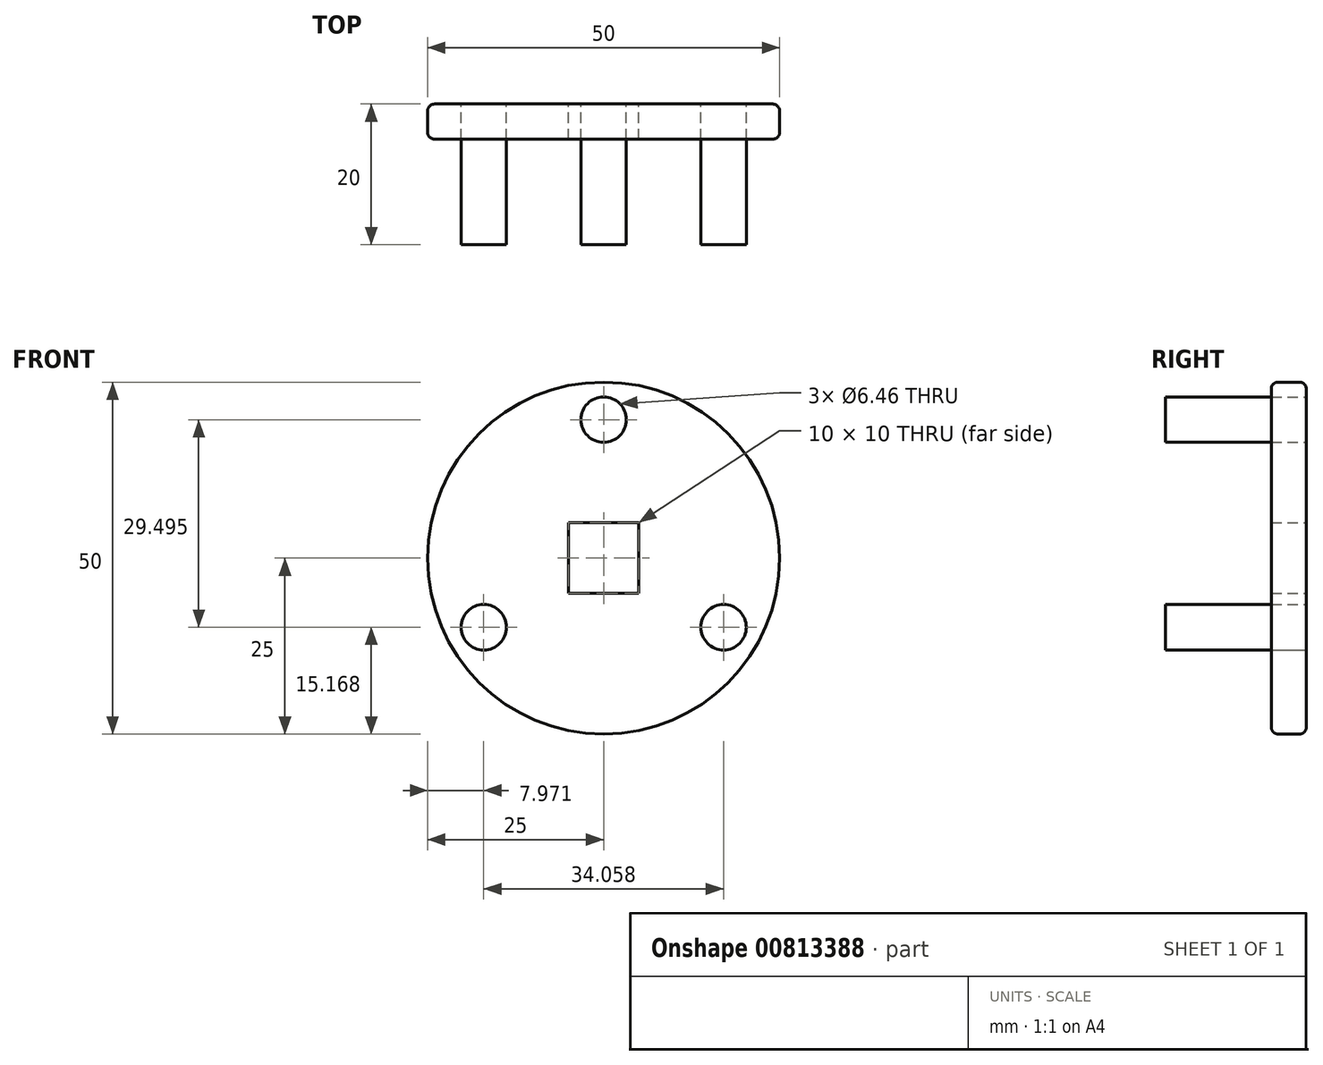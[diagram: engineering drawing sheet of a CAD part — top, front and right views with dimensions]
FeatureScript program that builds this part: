
annotation { "Feature Type Name" : "Feature", "Feature Type Description" : "" }
export const myFeature = defineFeature(function(context is Context, id is Id, definition is map)
    precondition{}
    {
        {
            var Q0;
            Q0=qCreatedBy(makeId("Front.planeOp"),FACE);
            var sketch = newSketch(context, id + "F0", { "sketchPlane" : qUnion([Q0])});
            skCircle(sketch, "E0", {"center": v(0, 0) * mm, "radius": 25 * mm});
            skCircle(sketch, "E1", {"center": v(0, 19.66) * mm, "radius": 3.23 * mm});
            skCircle(sketch, "E2.1.0", {"center": v(-17.03, -9.83) * mm, "radius": 3.23 * mm});
            skCircle(sketch, "E2.2.0", {"center": v(17.03, -9.83) * mm, "radius": 3.23 * mm});
            skLineSegment(sketch, "E3.bottom", {"start": v(-5, -5) * mm, "end": v(5, -5) * mm});
            skLineSegment(sketch, "E3.top", {"start": v(-5, 5) * mm, "end": v(5, 5) * mm});
            skLineSegment(sketch, "E3.left", {"start": v(-5, -5) * mm, "end": v(-5, 5) * mm});
            skLineSegment(sketch, "E3.right", {"start": v(5, -5) * mm, "end": v(5, 5) * mm});
            skSolve(sketch);
        }
        {
            var Q0;
            Q0=makeQuery(id+"F0.imprint","IMPRINT",FACE,{"disambiguationData":[TD([[makeQuery(id+"F0.imprint","IMPRINT",EDGE,{"derivedFrom":sQuery(id+"F0.wireOp",EDGE,"E2.2.0")}),1.0]])]});
            var Q1;
            Q1=makeQuery(id+"F0.imprint","IMPRINT",FACE,{"disambiguationData":[TD([[makeQuery(id+"F0.imprint","IMPRINT",EDGE,{"derivedFrom":sQuery(id+"F0.wireOp",EDGE,"E2.1.0")}),1.0]])]});
            var Q2;
            Q2=makeQuery(id+"F0.imprint","IMPRINT",FACE,{"disambiguationData":[TD([[makeQuery(id+"F0.imprint","IMPRINT",EDGE,{"derivedFrom":sQuery(id+"F0.wireOp",EDGE,"E1")}),1.0]])]});
            extrude(context, id + "F1", {"entities" : qUnion([Q0, Q1, Q2]), "depth" : 20 * mm, "offsetDistance" : 25.4 * mm});
        }
        {
            var Q0;
            Q0=makeQuery(id+"F0.imprint","IMPRINT",FACE,{"disambiguationData":[TD([[makeQuery(id+"F0.imprint","IMPRINT",EDGE,{"derivedFrom":sQuery(id+"F0.wireOp",EDGE,"E0")}),1.0]])]});
            extrude(context, id + "F2", {"entities" : qUnion([Q0]), "depth" : 5 * mm, "offsetDistance" : 25 * mm});
        }
        {
            var Q0;
            Q0=makeQuery(id+"F2.opExtrude","CAP_EDGE",EDGE,{"disambiguationData":[OSD([sQuery(id+"F0.wireOp",EDGE,"E0")])],"isStart":true});
            var Q1;
            Q1=makeQuery(id+"F2.opExtrude","CAP_EDGE",EDGE,{"disambiguationData":[OSD([sQuery(id+"F0.wireOp",EDGE,"E0")])],"isStart":false});
            fillet(context, id + "F3", {"entities" : qUnion([Q0, Q1]), "radius" : 1 * mm, "tangentPropagation" : true, "allowEdgeOverflow" : false});
        }
    });
